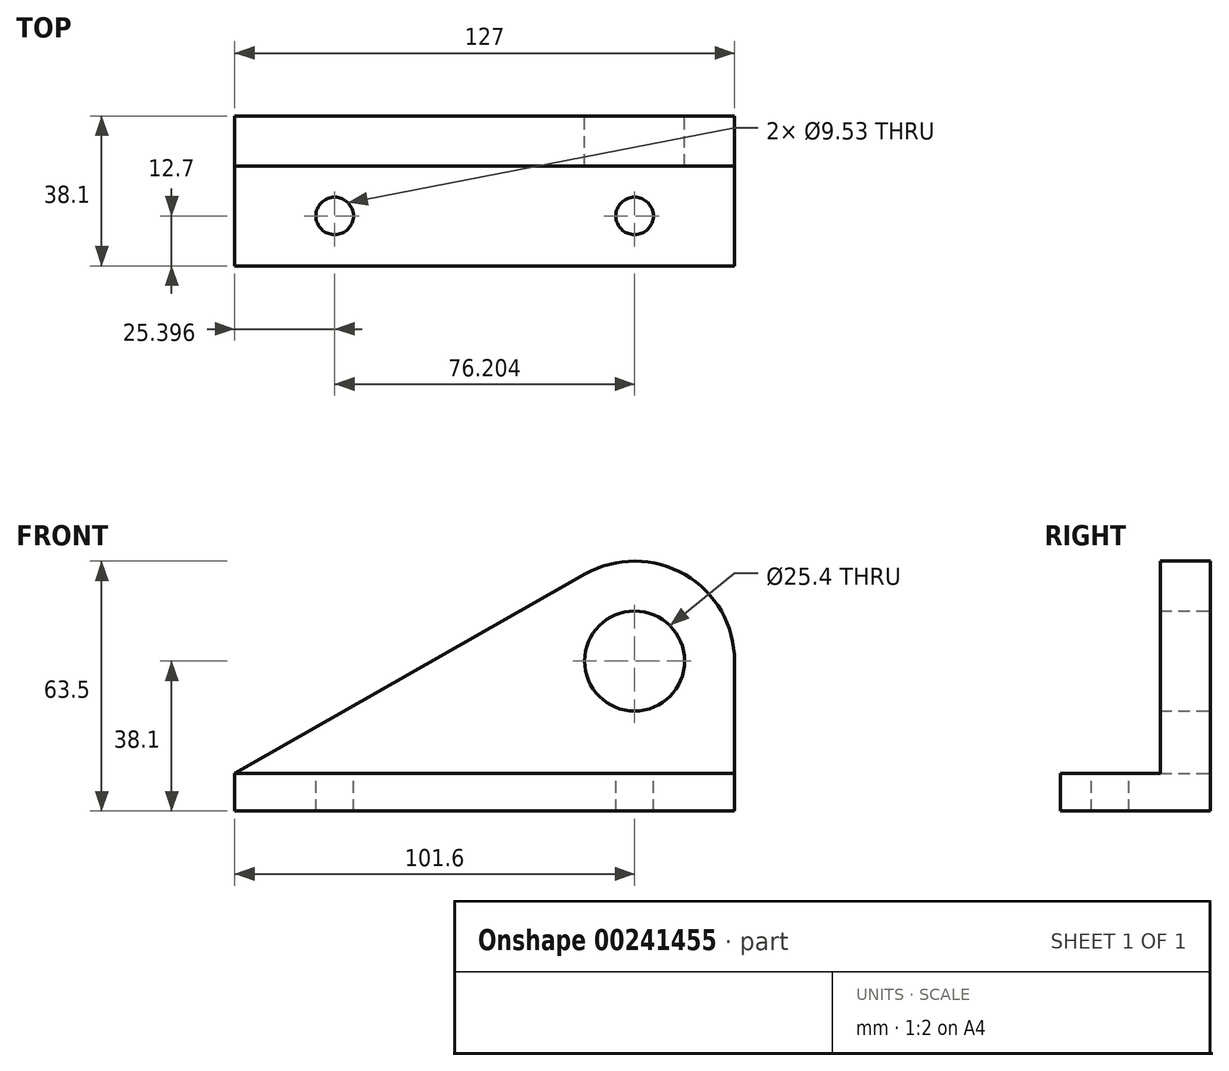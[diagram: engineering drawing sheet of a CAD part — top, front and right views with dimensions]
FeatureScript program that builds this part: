
annotation { "Feature Type Name" : "Feature", "Feature Type Description" : "" }
export const myFeature = defineFeature(function(context is Context, id is Id, definition is map)
    precondition{}
    {
        {
            var Q0;
            Q0=qCreatedBy(makeId("Front.planeOp"),FACE);
            var sketch = newSketch(context, id + "F0", { "sketchPlane" : qUnion([Q0])});
            skLineSegment(sketch, "E0", {"start": v(0, 0) * mm, "end": v(127, 0) * mm});
            skLineSegment(sketch, "E1", {"start": v(127, 0) * mm, "end": v(127, 9.52) * mm});
            skLineSegment(sketch, "E2", {"start": v(127, 9.52) * mm, "end": v(0, 9.52) * mm});
            skLineSegment(sketch, "E3", {"start": v(0, 9.52) * mm, "end": v(0, 0) * mm});
            skLineSegment(sketch, "E4", {"start": v(127, 9.52) * mm, "end": v(101.6, 9.52) * mm});
            skArc(sketch, "E5", {"start": v(127, 38.1) * mm, "mid": v(114.37, 60.06) * mm, "end": v(89.04, 60.18) * mm});
            skLineSegment(sketch, "E6", {"start": v(127, 9.52) * mm, "end": v(127, 38.1) * mm});
            skLineSegment(sketch, "E7", {"start": v(0, 9.52) * mm, "end": v(89.04, 60.18) * mm});
            skSolve(sketch);
        }
        {
            var Q0;
            Q0=makeQuery(id+"F0.imprint","IMPRINT",FACE,{"disambiguationData":[TD([[makeQuery(id+"F0.imprint","IMPRINT",EDGE,{"derivedFrom":sQuery(id+"F0.wireOp",EDGE,"E0")}),1.0]])]});
            extrude(context, id + "F1", {"entities" : qUnion([Q0]), "depth" : 38.1 * mm});
        }
        {
            var Q0;
            Q0=makeQuery(id+"F0.imprint","IMPRINT",FACE,{"disambiguationData":[TD([[makeQuery(id+"F0.imprint","IMPRINT",EDGE,{"derivedFrom":sQuery(id+"F0.wireOp",EDGE,"E2")}),-1.0]])]});
            extrude(context, id + "F2", {"entities" : qUnion([Q0]), "operationType" : NewBodyOperationType.ADD, "depth" : 12.7 * mm});
        }
        {
            var Q0;
            Q0=makeQuery(id+"F1.opExtrude","SWEPT_FACE",FACE,{"disambiguationData":[OSD([sQuery(id+"F0.wireOp",EDGE,"E2"),sQuery(id+"F0.wireOp",EDGE,"E4")])]});
            var sketch = newSketch(context, id + "F3", { "sketchPlane" : qUnion([Q0])});
            skLineSegment(sketch, "E8", {"start": v(0, -25.4) * mm, "end": v(25.4, -25.4) * mm});
            skLineSegment(sketch, "E9", {"start": v(25.4, -25.4) * mm, "end": v(101.6, -25.4) * mm});
            skSolve(sketch);
        }
        {
            var Q0;
            {var subQ0=sQuery(id+"F0.wireOp",EDGE,"E2");var subQ2=sQuery(id+"F0.wireOp",EDGE,"E4");var subQ3=makeQuery(id+"F1.opExtrude","CAP_EDGE",EDGE,{"disambiguationData":[OSD([subQ0,subQ2])],"isStart":false});Q0=makeQuery(id+"F3.imprint","IMPRINT",FACE,{"disambiguationData":[TD([[makeQuery(id+"F3.imprint","IMPRINT",EDGE,{"derivedFrom":subQ3}),-1.0]])]});}
            var sketch = newSketch(context, id + "F4", { "sketchPlane" : qUnion([Q0])});
            skCircle(sketch, "E10", {"center": v(25.4, -25.4) * mm, "radius": 4.76 * mm});
            skCircle(sketch, "E11", {"center": v(101.6, -25.4) * mm, "radius": 4.76 * mm});
            skSolve(sketch);
        }
        {
            var Q0;
            Q0=sQuery(id+"F4.wireOp",VERTEX,"E10.center");
            var Q1;
            Q1=makeQuery(id+"F1.opExtrude","SWEPT_BODY",BODY,{"disambiguationData":[OSD([sQuery(id+"F0.wireOp",EDGE,"E0"),sQuery(id+"F0.wireOp",EDGE,"E1"),sQuery(id+"F0.wireOp",EDGE,"E2"),sQuery(id+"F0.wireOp",EDGE,"E3"),sQuery(id+"F0.wireOp",EDGE,"E4")])]});
            hole(context, id + "F5", {"style" : HoleStyle.SIMPLE, "endStyle" : HoleEndStyle.THROUGH, "holeDiameter" : 9.52 * mm, "locations" : qUnion([Q0]), "scope" : qUnion([Q1]), "isTappedThrough" : true});
        }
        {
            var Q0;
            Q0=sQuery(id+"F3.wireOp",VERTEX,"E9.end");
            var Q1;
            Q1=makeQuery(id+"F1.opExtrude","SWEPT_BODY",BODY,{"disambiguationData":[OSD([sQuery(id+"F0.wireOp",EDGE,"E0"),sQuery(id+"F0.wireOp",EDGE,"E1"),sQuery(id+"F0.wireOp",EDGE,"E2"),sQuery(id+"F0.wireOp",EDGE,"E3"),sQuery(id+"F0.wireOp",EDGE,"E4")])]});
            hole(context, id + "F6", {"style" : HoleStyle.SIMPLE, "endStyle" : HoleEndStyle.THROUGH, "holeDiameter" : 9.52 * mm, "locations" : qUnion([Q0]), "scope" : qUnion([Q1]), "isTappedThrough" : true});
        }
        {
            var Q0;
            Q0=sQuery(id+"F0.wireOp",VERTEX,"E5.center");
            var Q1;
            Q1=makeQuery(id+"F1.opExtrude","SWEPT_BODY",BODY,{"disambiguationData":[OSD([sQuery(id+"F0.wireOp",EDGE,"E0"),sQuery(id+"F0.wireOp",EDGE,"E1"),sQuery(id+"F0.wireOp",EDGE,"E2"),sQuery(id+"F0.wireOp",EDGE,"E3"),sQuery(id+"F0.wireOp",EDGE,"E4")])]});
            hole(context, id + "F7", {"style" : HoleStyle.SIMPLE, "endStyle" : HoleEndStyle.THROUGH, "oppositeDirection" : true, "holeDiameter" : 25.4 * mm, "locations" : qUnion([Q0]), "scope" : qUnion([Q1]), "isTappedThrough" : true});
        }
    });
